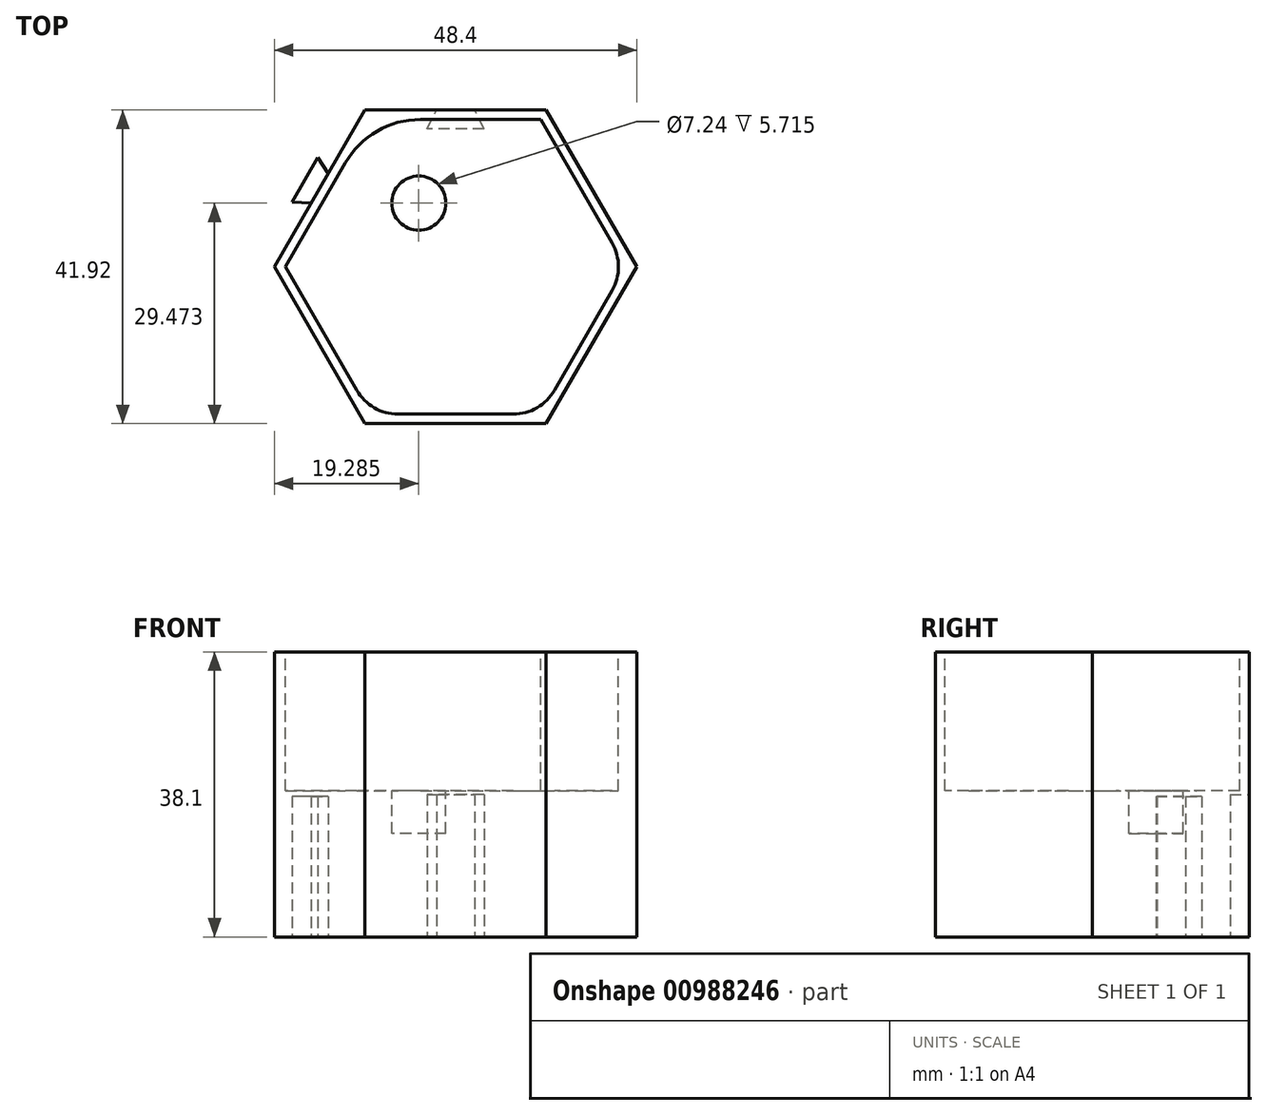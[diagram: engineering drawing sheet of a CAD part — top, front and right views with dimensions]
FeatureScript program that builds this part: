
annotation { "Feature Type Name" : "Feature", "Feature Type Description" : "" }
export const myFeature = defineFeature(function(context is Context, id is Id, definition is map)
    precondition{}
    {
        {
            var Q0;
            Q0=qCreatedBy(makeId("Top.planeOp"),FACE);
            var sketch = newSketch(context, id + "F0", { "sketchPlane" : qUnion([Q0])});
            skCircle(sketch, "E0.cCircle", {"center": v(0, 0) * mm, "radius": 20.96 * mm, "construction": true});
            skLineSegment(sketch, "E0.0", {"start": v(12.1, -20.96) * mm, "end": v(-12.1, -20.96) * mm});
            skLineSegment(sketch, "E0.1", {"start": v(-12.1, -20.96) * mm, "end": v(-24.2, 0) * mm});
            skLineSegment(sketch, "E0.2", {"start": v(-24.2, 0) * mm, "end": v(-12.1, 20.95) * mm});
            skLineSegment(sketch, "E0.3", {"start": v(-12.1, 20.95) * mm, "end": v(12.1, 20.96) * mm});
            skLineSegment(sketch, "E0.4", {"start": v(12.1, 20.96) * mm, "end": v(24.2, 0) * mm});
            skLineSegment(sketch, "E0.5", {"start": v(24.2, 0) * mm, "end": v(12.1, -20.96) * mm});
            skPoint(sketch, "E0.0.midPoint", {"position": v(0, -20.96) * mm});
            skSolve(sketch);
        }
        {
            var Q0;
            Q0 = qSketchRegion(id + "F0", true);
            extrude(context, id + "F1", {"entities" : qUnion([Q0]), "depth" : 38.1 * mm, "offsetDistance" : 25.4 * mm});
        }
        {
            var Q0;
            Q0=makeQuery(id+"F1.opExtrude","CAP_FACE",FACE,{"disambiguationData":[OSD([sQuery(id+"F0.wireOp",EDGE,"E0.0"),sQuery(id+"F0.wireOp",EDGE,"E0.1"),sQuery(id+"F0.wireOp",EDGE,"E0.2"),sQuery(id+"F0.wireOp",EDGE,"E0.3"),sQuery(id+"F0.wireOp",EDGE,"E0.4"),sQuery(id+"F0.wireOp",EDGE,"E0.5")])],"isStart":false});
            var sketch = newSketch(context, id + "F2", { "sketchPlane" : qUnion([Q0])});
            skCircle(sketch, "E1.cCircle", {"center": v(0, 0) * mm, "radius": 19.69 * mm, "construction": true});
            skLineSegment(sketch, "E1.0", {"start": v(11.37, -19.69) * mm, "end": v(-11.37, -19.69) * mm});
            skLineSegment(sketch, "E1.1", {"start": v(-11.37, -19.69) * mm, "end": v(-22.73, 0) * mm});
            skLineSegment(sketch, "E1.2", {"start": v(-22.73, 0) * mm, "end": v(-11.37, 19.68) * mm});
            skLineSegment(sketch, "E1.3", {"start": v(-11.37, 19.68) * mm, "end": v(11.37, 19.69) * mm});
            skLineSegment(sketch, "E1.4", {"start": v(11.37, 19.69) * mm, "end": v(22.73, 0) * mm});
            skLineSegment(sketch, "E1.5", {"start": v(22.73, 0) * mm, "end": v(11.37, -19.69) * mm});
            skPoint(sketch, "E1.0.midPoint", {"position": v(0, -19.69) * mm});
            skSolve(sketch);
        }
        {
            var Q0;
            Q0=makeQuery(id+"F2.imprint","IMPRINT",FACE,{"disambiguationData":[TD([[makeQuery(id+"F2.imprint","IMPRINT",EDGE,{"derivedFrom":sQuery(id+"F2.wireOp",EDGE,"E1.0")}),-1.0]])]});
            extrude(context, id + "F3", {"entities" : qUnion([Q0]), "operationType" : NewBodyOperationType.REMOVE, "oppositeDirection" : true, "depth" : 18.54 * mm, "offsetDistance" : 25.4 * mm});
        }
        {
            var Q0;
            Q0=makeQuery(id+"F1.opExtrude","CAP_FACE",FACE,{"disambiguationData":[OSD([sQuery(id+"F0.wireOp",EDGE,"E0.0"),sQuery(id+"F0.wireOp",EDGE,"E0.1"),sQuery(id+"F0.wireOp",EDGE,"E0.2"),sQuery(id+"F0.wireOp",EDGE,"E0.3"),sQuery(id+"F0.wireOp",EDGE,"E0.4"),sQuery(id+"F0.wireOp",EDGE,"E0.5")])],"isStart":false});
            var sketch = newSketch(context, id + "F4", { "sketchPlane" : qUnion([Q0])});
            skCircle(sketch, "E2", {"center": v(-4.7, 8.13) * mm, "radius": 11.56 * mm});
            skCircle(sketch, "E3", {"center": v(7.7, -13.34) * mm, "radius": 6.35 * mm});
            skCircle(sketch, "E4", {"center": v(15.4, 0) * mm, "radius": 6.35 * mm});
            skCircle(sketch, "E5", {"center": v(-7.7, -13.34) * mm, "radius": 6.35 * mm});
            skCircle(sketch, "E6", {"center": v(-4.7, 8.13) * mm, "radius": 3.81 * mm});
            skSolve(sketch);
        }
        {
            var Q0;
            {var subQ13=sQuery(id+"F4.wireOp",EDGE,"E2");var subQ14=makeQuery(id+"F3.boolean.opBoolean","COPY",EDGE,{"derivedFrom":makeQuery(id+"F3.opExtrude","CAP_EDGE",EDGE,{"disambiguationData":[OSD([sQuery(id+"F2.wireOp",EDGE,"E1.2")])],"isStart":true})});var subQ15=makeQuery(id+"F4.imprint","INTERSECT",VERTEX,{"derivedFrom":[subQ14,subQ13]});Q0=makeQuery(id+"F4.imprint","IMPRINT",FACE,{"disambiguationData":[TD([[makeQuery(id+"F4.imprint","IMPRINT",EDGE,{"disambiguationData":[TD([[subQ15,-1.0]])],"derivedFrom":subQ13}),-1.0]])]});}
            var Q1;
            {var subQ0=sQuery(id+"F4.wireOp",EDGE,"E5");var subQ1=makeQuery(id+"F3.boolean.opBoolean","COPY",EDGE,{"derivedFrom":makeQuery(id+"F3.opExtrude","CAP_EDGE",EDGE,{"disambiguationData":[OSD([sQuery(id+"F2.wireOp",EDGE,"E1.0")])],"isStart":true})});var subQ2=makeQuery(id+"F4.imprint","INTERSECT",VERTEX,{"derivedFrom":[subQ1,subQ0]});Q1=makeQuery(id+"F4.imprint","IMPRINT",FACE,{"disambiguationData":[TD([[makeQuery(id+"F4.imprint","IMPRINT",EDGE,{"disambiguationData":[TD([[subQ2,1.0]])],"derivedFrom":subQ0}),-1.0]])]});}
            var Q2;
            {var subQ0=sQuery(id+"F4.wireOp",EDGE,"E3");var subQ1=makeQuery(id+"F3.boolean.opBoolean","COPY",EDGE,{"derivedFrom":makeQuery(id+"F3.opExtrude","CAP_EDGE",EDGE,{"disambiguationData":[OSD([sQuery(id+"F2.wireOp",EDGE,"E1.0")])],"isStart":true})});var subQ2=makeQuery(id+"F4.imprint","INTERSECT",VERTEX,{"derivedFrom":[subQ1,subQ0]});Q2=makeQuery(id+"F4.imprint","IMPRINT",FACE,{"disambiguationData":[TD([[makeQuery(id+"F4.imprint","IMPRINT",EDGE,{"disambiguationData":[TD([[subQ2,-1.0]])],"derivedFrom":subQ0}),-1.0]])]});}
            var Q3;
            {var subQ0=sQuery(id+"F4.wireOp",EDGE,"E4");var subQ1=makeQuery(id+"F3.boolean.opBoolean","COPY",EDGE,{"derivedFrom":makeQuery(id+"F3.opExtrude","CAP_EDGE",EDGE,{"disambiguationData":[OSD([sQuery(id+"F2.wireOp",EDGE,"E1.4")])],"isStart":true})});var subQ2=makeQuery(id+"F4.imprint","INTERSECT",VERTEX,{"derivedFrom":[subQ1,subQ0]});Q3=makeQuery(id+"F4.imprint","IMPRINT",FACE,{"disambiguationData":[TD([[makeQuery(id+"F4.imprint","IMPRINT",EDGE,{"disambiguationData":[TD([[subQ2,1.0]])],"derivedFrom":subQ0}),-1.0]])]});}
            var Q4;
            {var subQ0=sQuery(id+"F4.wireOp",EDGE,"E2");var subQ1=makeQuery(id+"F3.boolean.opBoolean","COPY",EDGE,{"derivedFrom":makeQuery(id+"F3.opExtrude","CAP_EDGE",EDGE,{"disambiguationData":[OSD([sQuery(id+"F2.wireOp",EDGE,"E1.2")])],"isStart":true})});var subQ2=makeQuery(id+"F4.imprint","INTERSECT",VERTEX,{"derivedFrom":[subQ1,subQ0]});Q4=makeQuery(id+"F4.imprint","IMPRINT",FACE,{"disambiguationData":[TD([[makeQuery(id+"F4.imprint","IMPRINT",EDGE,{"disambiguationData":[TD([[subQ2,1.0]])],"derivedFrom":subQ0}),-1.0]])]});}
            extrude(context, id + "F5", {"entities" : qUnion([Q0, Q1, Q2, Q3, Q4]), "operationType" : NewBodyOperationType.ADD, "oppositeDirection" : true, "depth" : 18.8 * mm, "offsetDistance" : 25.4 * mm});
        }
        {
            var Q0;
            {var subQ0=sQuery(id+"F4.wireOp",EDGE,"E5");var subQ1=sQuery(id+"F2.wireOp",EDGE,"E1.1");var subQ2=sQuery(id+"F2.wireOp",EDGE,"E1.0");var subQ3=sQuery(id+"F4.wireOp",EDGE,"E4");var subQ4=sQuery(id+"F2.wireOp",EDGE,"E1.5");var subQ5=sQuery(id+"F2.wireOp",EDGE,"E1.4");var subQ6=sQuery(id+"F4.wireOp",EDGE,"E3");var subQ7=sQuery(id+"F4.wireOp",EDGE,"E2");var subQ8=sQuery(id+"F2.wireOp",EDGE,"E1.3");var subQ9=sQuery(id+"F2.wireOp",EDGE,"E1.2");Q0=makeQuery(id+"F5.boolean.opBoolean","MERGE",FACE,{"derivedFrom":[makeQuery(id+"F1.opExtrude","CAP_FACE",FACE,{"disambiguationData":[OSD([sQuery(id+"F0.wireOp",EDGE,"E0.0"),sQuery(id+"F0.wireOp",EDGE,"E0.1"),sQuery(id+"F0.wireOp",EDGE,"E0.2"),sQuery(id+"F0.wireOp",EDGE,"E0.3"),sQuery(id+"F0.wireOp",EDGE,"E0.4"),sQuery(id+"F0.wireOp",EDGE,"E0.5")])],"isStart":false}),makeQuery(id+"F5.opExtrude","CAP_FACE",FACE,{"disambiguationData":[OSD([subQ9,subQ8,subQ7])],"isStart":true}),makeQuery(id+"F5.opExtrude","CAP_FACE",FACE,{"disambiguationData":[OSD([subQ2,subQ1,subQ9,subQ8,subQ5,subQ4,subQ7,subQ6,subQ3,subQ0])],"isStart":true}),makeQuery(id+"F5.opExtrude","CAP_FACE",FACE,{"disambiguationData":[OSD([subQ2,subQ4,subQ6])],"isStart":true}),makeQuery(id+"F5.opExtrude","CAP_FACE",FACE,{"disambiguationData":[OSD([subQ5,subQ4,subQ3])],"isStart":true}),makeQuery(id+"F5.opExtrude","CAP_FACE",FACE,{"disambiguationData":[OSD([subQ2,subQ1,subQ0])],"isStart":true})]});}
            var sketch = newSketch(context, id + "F6", { "sketchPlane" : qUnion([Q0])});
            skCircle(sketch, "E7", {"center": v(-4.91, 8.51) * mm, "radius": 3.62 * mm});
            skSolve(sketch);
        }
        {
            var Q0;
            Q0 = qSketchRegion(id + "F6", true);
            extrude(context, id + "F7", {"entities" : qUnion([Q0]), "operationType" : NewBodyOperationType.REMOVE, "oppositeDirection" : true, "depth" : 24.26 * mm, "offsetDistance" : 25.4 * mm});
        }
        {
            var Q0;
            Q0=makeQuery(id+"F1.opExtrude","CAP_FACE",FACE,{"disambiguationData":[OSD([sQuery(id+"F0.wireOp",EDGE,"E0.0"),sQuery(id+"F0.wireOp",EDGE,"E0.1"),sQuery(id+"F0.wireOp",EDGE,"E0.2"),sQuery(id+"F0.wireOp",EDGE,"E0.3"),sQuery(id+"F0.wireOp",EDGE,"E0.4"),sQuery(id+"F0.wireOp",EDGE,"E0.5")])],"isStart":true});
            var sketch = newSketch(context, id + "F8", { "sketchPlane" : qUnion([Q0])});
            skLineSegment(sketch, "E8", {"start": v(-18.15, -10.48) * mm, "end": v(18.15, 10.48) * mm});
            skLineSegment(sketch, "E9", {"start": v(18.15, -10.48) * mm, "end": v(-18.15, 10.48) * mm});
            skLineSegment(sketch, "E10", {"start": v(0, -20.96) * mm, "end": v(0, 20.96) * mm});
            skLineSegment(sketch, "E11", {"start": v(-12.1, -20.95) * mm, "end": v(12.1, 20.96) * mm});
            skLineSegment(sketch, "E12", {"start": v(12.1, -20.96) * mm, "end": v(-12.1, 20.96) * mm});
            skLineSegment(sketch, "E13", {"start": v(-24.2, 0) * mm, "end": v(24.2, 0) * mm});
            skLineSegment(sketch, "E14", {"start": v(0, -20.96) * mm, "end": v(0, -18.41) * mm});
            skLineSegment(sketch, "E15", {"start": v(0, -20.96) * mm, "end": v(-3.8, -20.96) * mm});
            skLineSegment(sketch, "E16", {"start": v(0, -18.41) * mm, "end": v(-2.54, -18.41) * mm});
            skLineSegment(sketch, "E17", {"start": v(-2.54, -18.41) * mm, "end": v(-3.8, -20.96) * mm});
            skLineSegment(sketch, "E18.MirrorCS", {"start": v(0, -18.41) * mm, "end": v(2.54, -18.41) * mm});
            skLineSegment(sketch, "E19.MirrorCS", {"start": v(2.54, -18.41) * mm, "end": v(3.8, -20.96) * mm});
            skLineSegment(sketch, "E20.MirrorCS", {"start": v(0, -20.96) * mm, "end": v(3.8, -20.96) * mm});
            skLineSegment(sketch, "E21", {"start": v(-18.15, -10.48) * mm, "end": v(-20.13, -11.62) * mm});
            skLineSegment(sketch, "E22", {"start": v(-20.13, -11.62) * mm, "end": v(-18.41, -14.6) * mm});
            skLineSegment(sketch, "E23", {"start": v(-18.15, -10.48) * mm, "end": v(-17, -12.46) * mm});
            skLineSegment(sketch, "E24", {"start": v(-17, -12.46) * mm, "end": v(-18.41, -14.6) * mm});
            skLineSegment(sketch, "E25.MirrorCS", {"start": v(-20.13, -11.62) * mm, "end": v(-21.84, -8.65) * mm});
            skLineSegment(sketch, "E26.MirrorCS", {"start": v(-19.3, -8.5) * mm, "end": v(-21.84, -8.65) * mm});
            skLineSegment(sketch, "E27.MirrorCS", {"start": v(-18.15, -10.48) * mm, "end": v(-19.3, -8.5) * mm});
            skSolve(sketch);
        }
        {
            var Q0;
            Q0=makeQuery(id+"F8.imprint","IMPRINT",FACE,{"disambiguationData":[TD([[makeQuery(id+"F8.imprint","IMPRINT",EDGE,{"derivedFrom":sQuery(id+"F8.wireOp",EDGE,"E21")}),-1.0]])]});
            var Q1;
            Q1=makeQuery(id+"F8.imprint","IMPRINT",FACE,{"disambiguationData":[TD([[makeQuery(id+"F8.imprint","IMPRINT",EDGE,{"derivedFrom":sQuery(id+"F8.wireOp",EDGE,"E21")}),1.0]])]});
            extrude(context, id + "F9", {"entities" : qUnion([Q0, Q1]), "operationType" : NewBodyOperationType.ADD, "oppositeDirection" : true, "depth" : 18.8 * mm, "offsetDistance" : 25.4 * mm});
        }
        {
            var Q0;
            Q0=makeQuery(id+"F9.boolean.opBoolean","MERGE",FACE,{"derivedFrom":[makeQuery(id+"F1.opExtrude","CAP_FACE",FACE,{"disambiguationData":[OSD([sQuery(id+"F0.wireOp",EDGE,"E0.0"),sQuery(id+"F0.wireOp",EDGE,"E0.1"),sQuery(id+"F0.wireOp",EDGE,"E0.2"),sQuery(id+"F0.wireOp",EDGE,"E0.3"),sQuery(id+"F0.wireOp",EDGE,"E0.4"),sQuery(id+"F0.wireOp",EDGE,"E0.5")])],"isStart":true}),makeQuery(id+"F9.opExtrude","CAP_FACE",FACE,{"disambiguationData":[OSD([sQuery(id+"F8.wireOp",EDGE,"E22"),sQuery(id+"F8.wireOp",EDGE,"E23"),sQuery(id+"F8.wireOp",EDGE,"E24"),sQuery(id+"F8.wireOp",EDGE,"E25.MirrorCS"),sQuery(id+"F8.wireOp",EDGE,"E26.MirrorCS"),sQuery(id+"F8.wireOp",EDGE,"E27.MirrorCS")])],"isStart":true})]});
            var sketch = newSketch(context, id + "F10", { "sketchPlane" : qUnion([Q0])});
            skLineSegment(sketch, "E28", {"start": v(0, -20.96) * mm, "end": v(0, 20.96) * mm});
            skLineSegment(sketch, "E29", {"start": v(0, -20.96) * mm, "end": v(0, -18.41) * mm});
            skLineSegment(sketch, "E30", {"start": v(0, -20.96) * mm, "end": v(-2.54, -20.96) * mm});
            skLineSegment(sketch, "E31", {"start": v(0, -18.41) * mm, "end": v(-3.8, -18.41) * mm});
            skLineSegment(sketch, "E32", {"start": v(-3.8, -18.41) * mm, "end": v(-2.54, -20.96) * mm});
            skLineSegment(sketch, "E33.MirrorCS", {"start": v(0, -18.41) * mm, "end": v(3.81, -18.41) * mm});
            skLineSegment(sketch, "E34.MirrorCS", {"start": v(3.81, -18.41) * mm, "end": v(2.54, -20.96) * mm});
            skLineSegment(sketch, "E35.MirrorCS", {"start": v(0, -20.96) * mm, "end": v(2.54, -20.96) * mm});
            skSolve(sketch);
        }
        {
            var Q0;
            {var subQ0=sQuery(id+"F10.wireOp",EDGE,"E33.MirrorCS");var subQ4=sQuery(id+"F10.wireOp",EDGE,"E30");Q0=qUnion([makeQuery(id+"F10.imprint","IMPRINT",FACE,{"disambiguationData":[TD([[makeQuery(id+"F10.imprint","IMPRINT",EDGE,{"derivedFrom":subQ4}),1.0]])]}),makeQuery(id+"F10.imprint","IMPRINT",FACE,{"disambiguationData":[TD([[makeQuery(id+"F10.imprint","IMPRINT",EDGE,{"derivedFrom":subQ0}),-1.0]])]})]);}
            extrude(context, id + "F11", {"entities" : qUnion([Q0]), "operationType" : NewBodyOperationType.REMOVE, "oppositeDirection" : true, "depth" : 19.05 * mm, "offsetDistance" : 25.4 * mm});
        }
    });
